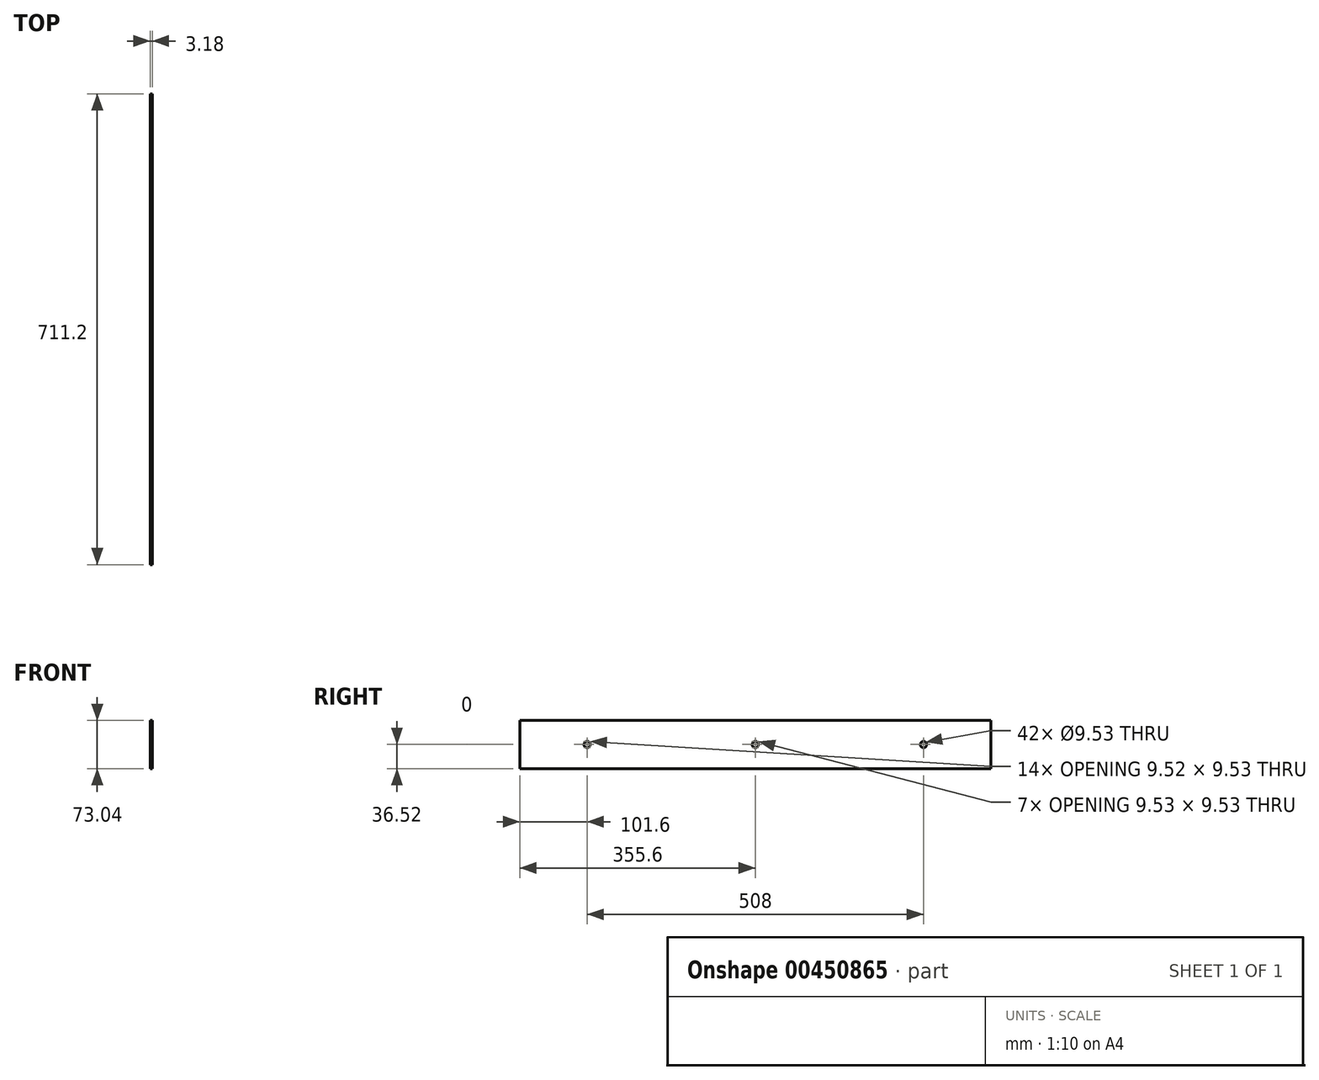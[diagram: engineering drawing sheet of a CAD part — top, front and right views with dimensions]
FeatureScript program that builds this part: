
annotation { "Feature Type Name" : "Feature", "Feature Type Description" : "" }
export const myFeature = defineFeature(function(context is Context, id is Id, definition is map)
    precondition{}
    {
        {
            var Q0;
            Q0=qCreatedBy(makeId("Right.planeOp"),FACE);
            var sketch = newSketch(context, id + "F0", { "sketchPlane" : qUnion([Q0])});
            skLineSegment(sketch, "E0.bottom", {"start": v(355.6, -36.52) * mm, "end": v(-355.6, -36.52) * mm});
            skLineSegment(sketch, "E0.top", {"start": v(355.6, 36.52) * mm, "end": v(-355.6, 36.52) * mm});
            skLineSegment(sketch, "E0.left", {"start": v(355.6, -36.52) * mm, "end": v(355.6, 36.52) * mm});
            skLineSegment(sketch, "E0.right", {"start": v(-355.6, -36.52) * mm, "end": v(-355.6, 36.52) * mm});
            skPoint(sketch, "E0.middle", {"position": v(0, 0) * mm});
            skSolve(sketch);
        }
        {
            var Q0;
            Q0=qSketchRegion(id+"F0",true);
            extrude(context, id + "F1", {"entities" : qUnion([Q0]), "depth" : 3.17 * mm});
        }
        {
            var Q0;
            Q0=makeQuery(id+"F1.opExtrude","CAP_FACE",FACE,{"disambiguationData":[OSD([sQuery(id+"F0.wireOp",EDGE,"E0.bottom"),sQuery(id+"F0.wireOp",EDGE,"E0.top"),sQuery(id+"F0.wireOp",EDGE,"E0.left"),sQuery(id+"F0.wireOp",EDGE,"E0.right")])],"isStart":true});
            var sketch = newSketch(context, id + "F2", { "sketchPlane" : qUnion([Q0])});
            skCircle(sketch, "E1", {"center": v(-254, 0) * mm, "radius": 4.76 * mm});
            skCircle(sketch, "E2", {"center": v(0, 0) * mm, "radius": 4.76 * mm});
            skCircle(sketch, "E3", {"center": v(254, 0) * mm, "radius": 4.76 * mm});
            skSolve(sketch);
        }
        {
            var Q0;
            Q0=qSketchRegion(id+"F2",true);
            extrude(context, id + "F3", {"entities" : qUnion([Q0]), "operationType" : NewBodyOperationType.REMOVE, "endBound" : BoundingType.UP_TO_NEXT, "oppositeDirection" : true, "depth" : 25.4 * mm});
        }
    });
